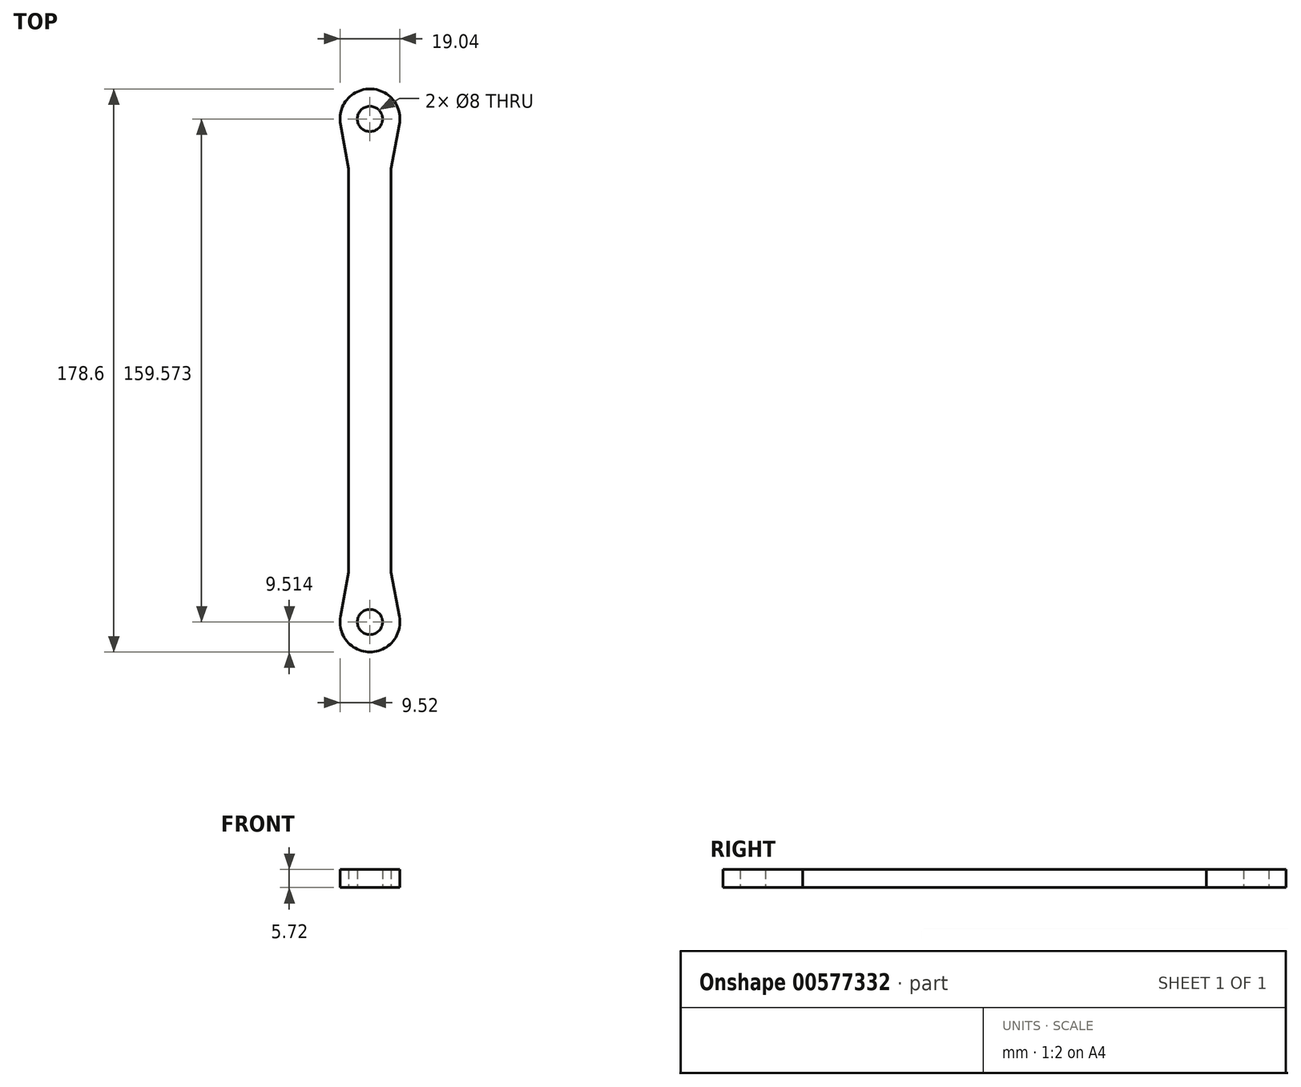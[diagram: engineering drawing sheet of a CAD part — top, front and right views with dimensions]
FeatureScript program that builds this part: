
annotation { "Feature Type Name" : "Feature", "Feature Type Description" : "" }
export const myFeature = defineFeature(function(context is Context, id is Id, definition is map)
    precondition{}
    {
        {
            var Q0;
            Q0=qCreatedBy(makeId("Top.planeOp"),FACE);
            var sketch = newSketch(context, id + "F0", { "sketchPlane" : qUnion([Q0])});
            skArc(sketch, "E0", {"start": v(0, -83.79) * mm, "mid": v(4, -79.79) * mm, "end": v(0, -75.79) * mm});
            skLineSegment(sketch, "E1", {"start": v(0, -89.3) * mm, "end": v(0, -83.79) * mm});
            skLineSegment(sketch, "E2", {"start": v(0, 0) * mm, "end": v(6.73, 0) * mm});
            skLineSegment(sketch, "E3", {"start": v(6.73, 0) * mm, "end": v(6.73, -63.98) * mm});
            skArc(sketch, "E4", {"start": v(0, -89.3) * mm, "mid": v(7.32, -85.87) * mm, "end": v(9.35, -78.04) * mm});
            skLineSegment(sketch, "E5", {"start": v(6.73, -63.98) * mm, "end": v(9.35, -78.04) * mm});
            skPoint(sketch, "E6.orphan", {"position": v(0, -92.06) * mm});
            skLineSegment(sketch, "E7.trimOffspring", {"start": v(0, -75.79) * mm, "end": v(0, 0) * mm});
            skSolve(sketch);
        }
        {
            var Q0;
            Q0 = qSketchRegion(id + "F0", true);
            extrude(context, id + "F1", {"entities" : qUnion([Q0]), "endBound" : BoundingType.SYMMETRIC, "depth" : 5.7 * mm, "offsetDistance" : 25.4 * mm});
        }
        {
            var Q0;
            Q0=makeQuery(id+"F1.opExtrude","SWEPT_BODY",BODY,{"disambiguationData":[OSD([sQuery(id+"F0.wireOp",EDGE,"E0"),sQuery(id+"F0.wireOp",EDGE,"E1"),sQuery(id+"F0.wireOp",EDGE,"E2"),sQuery(id+"F0.wireOp",EDGE,"E3"),sQuery(id+"F0.wireOp",EDGE,"E4"),sQuery(id+"F0.wireOp",EDGE,"E5"),sQuery(id+"F0.wireOp",EDGE,"E7.trimOffspring")])]});
            var Q1;
            Q1=qCreatedBy(makeId("Right.planeOp"),FACE);
            mirror(context, id + "F2", {"operationType" : NewBodyOperationType.ADD, "entities" : qUnion([Q0]), "mirrorPlane" : qUnion([Q1])});
        }
        {
            var Q0;
            Q0=makeQuery(id+"F1.opExtrude","SWEPT_BODY",BODY,{"disambiguationData":[OSD([sQuery(id+"F0.wireOp",EDGE,"E0"),sQuery(id+"F0.wireOp",EDGE,"E1"),sQuery(id+"F0.wireOp",EDGE,"E2"),sQuery(id+"F0.wireOp",EDGE,"E3"),sQuery(id+"F0.wireOp",EDGE,"E4"),sQuery(id+"F0.wireOp",EDGE,"E5"),sQuery(id+"F0.wireOp",EDGE,"E7.trimOffspring")])]});
            var Q1;
            Q1=qCreatedBy(makeId("Front.planeOp"),FACE);
            mirror(context, id + "F3", {"operationType" : NewBodyOperationType.ADD, "entities" : qUnion([Q0]), "mirrorPlane" : qUnion([Q1])});
        }
    });
